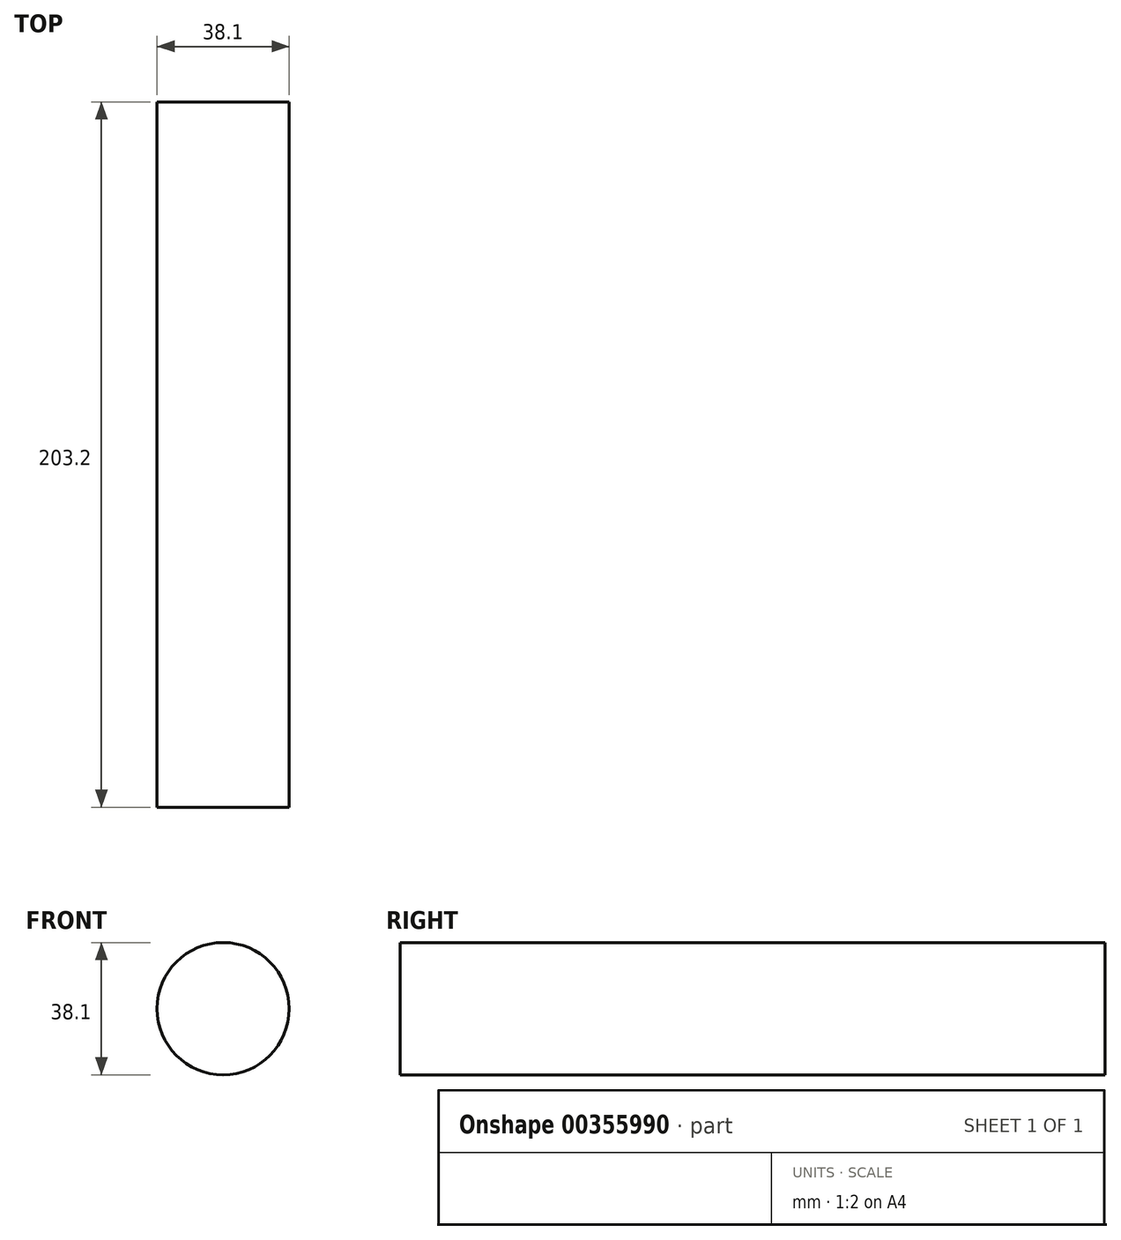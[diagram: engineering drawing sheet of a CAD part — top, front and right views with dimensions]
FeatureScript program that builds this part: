
annotation { "Feature Type Name" : "Feature", "Feature Type Description" : "" }
export const myFeature = defineFeature(function(context is Context, id is Id, definition is map)
    precondition{}
    {
        {
            var Q0;
            Q0=qCreatedBy(makeId("Front.planeOp"),FACE);
            var sketch = newSketch(context, id + "F0", { "sketchPlane" : qUnion([Q0])});
            skCircle(sketch, "E0", {"center": v(0, 0) * mm, "radius": 19.05 * mm});
            skCircle(sketch, "E1", {"center": v(0, 0) * mm, "radius": 15.88 * mm});
            skSolve(sketch);
        }
        {
            var Q0;
            Q0=qSketchRegion(id+"F0",true);
            var Q1;
            Q1=makeQuery(id+"F0.imprint","IMPRINT",FACE,{"disambiguationData":[TD([[makeQuery(id+"F0.imprint","IMPRINT",EDGE,{"derivedFrom":sQuery(id+"F0.wireOp",EDGE,"E1")}),1.0]])]});
            extrude(context, id + "F1", {"entities" : qUnion([Q0, Q1]), "depth" : 203.2 * mm});
        }
        {
            var Q0;
            Q0=makeQuery(id+"F1.opExtrude","CAP_FACE",FACE,{"disambiguationData":[OSD([sQuery(id+"F0.wireOp",EDGE,"E0")])],"isStart":true});
            extrude(context, id + "F2", {"entities" : qUnion([Q0]), "operationType" : NewBodyOperationType.REMOVE, "oppositeDirection" : true, "depth" : 25.4 * mm});
        }
        {
            var Q0;
            Q0=makeQuery(id+"F2.boolean.opBoolean","COPY",FACE,{"derivedFrom":makeQuery(id+"F2.opExtrude","CAP_FACE",FACE,{"disambiguationData":[OSD([sQuery(id+"F0.wireOp",EDGE,"E0")])],"isStart":false})});
            extrude(context, id + "F3", {"entities" : qUnion([Q0]), "operationType" : NewBodyOperationType.ADD, "depth" : 25.4 * mm});
        }
    });
